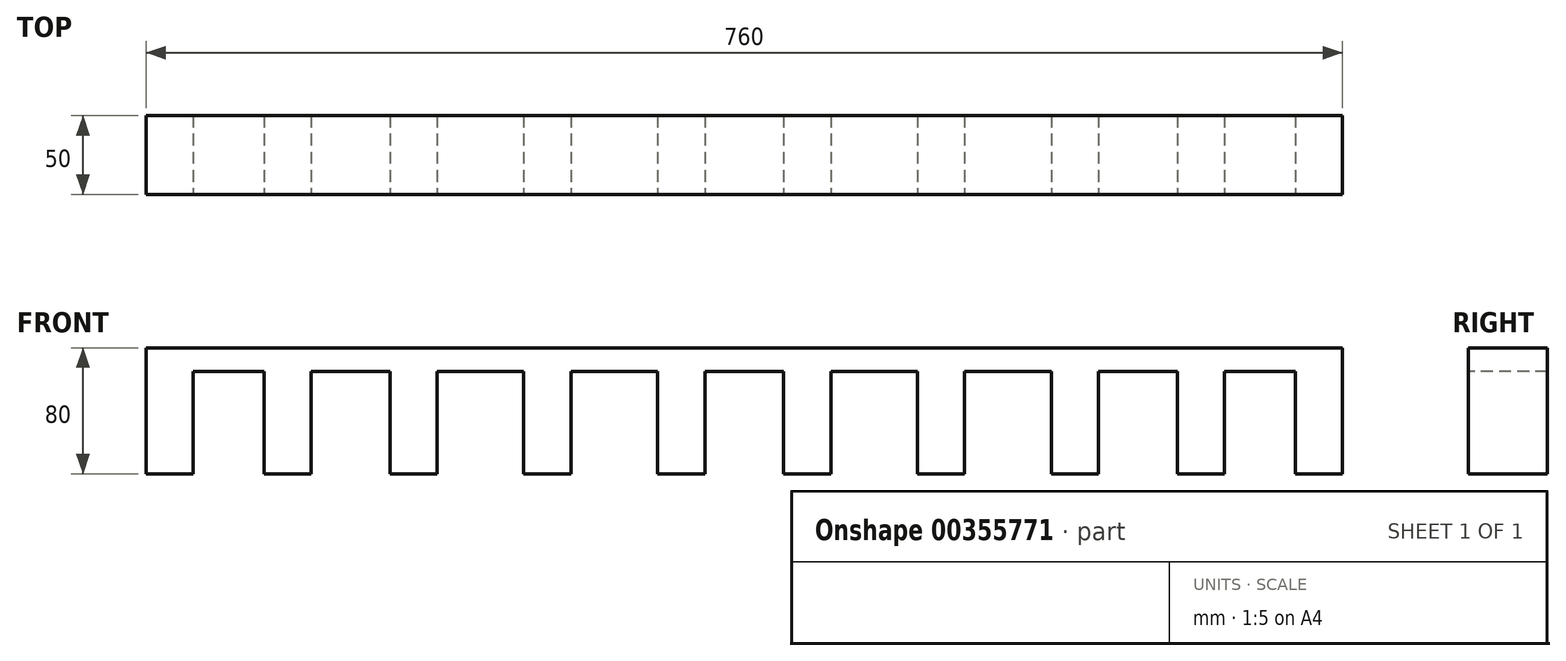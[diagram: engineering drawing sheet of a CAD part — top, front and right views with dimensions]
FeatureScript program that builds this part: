
annotation { "Feature Type Name" : "Feature", "Feature Type Description" : "" }
export const myFeature = defineFeature(function(context is Context, id is Id, definition is map)
    precondition{}
    {
        {
            var Q0;
            Q0=qCreatedBy(makeId("Front.planeOp"),FACE);
            var sketch = newSketch(context, id + "F0", { "sketchPlane" : qUnion([Q0])});
            skLineSegment(sketch, "E0.bottom", {"start": v(-404.78, 0) * mm, "end": v(355.22, 0) * mm});
            skLineSegment(sketch, "E0.top", {"start": v(-404.78, -80) * mm, "end": v(355.22, -80) * mm});
            skLineSegment(sketch, "E0.left", {"start": v(-404.78, 0) * mm, "end": v(-404.78, -80) * mm});
            skLineSegment(sketch, "E0.right", {"start": v(355.22, 0) * mm, "end": v(355.22, -80) * mm});
            skSolve(sketch);
        }
        {
            var Q0;
            Q0=makeQuery(id+"F0.imprint","IMPRINT",FACE,{"disambiguationData":[TD([[makeQuery(id+"F0.imprint","IMPRINT",EDGE,{"derivedFrom":sQuery(id+"F0.wireOp",EDGE,"E0.bottom")}),-1.0]])]});
            extrude(context, id + "F1", {"entities" : qUnion([Q0]), "depth" : 50 * mm});
        }
        {
            var Q0;
            Q0=makeQuery(id+"F1.opExtrude","CAP_FACE",FACE,{"disambiguationData":[OSD([sQuery(id+"F0.wireOp",EDGE,"E0.bottom"),sQuery(id+"F0.wireOp",EDGE,"E0.top"),sQuery(id+"F0.wireOp",EDGE,"E0.left"),sQuery(id+"F0.wireOp",EDGE,"E0.right")])],"isStart":false});
            var sketch = newSketch(context, id + "F2", { "sketchPlane" : qUnion([Q0])});
            skLineSegment(sketch, "E1.bottom", {"start": v(-374.78, -80) * mm, "end": v(-329.78, -80) * mm});
            skLineSegment(sketch, "E1.top", {"start": v(-374.78, -15) * mm, "end": v(-329.78, -15) * mm});
            skLineSegment(sketch, "E1.left", {"start": v(-374.78, -80) * mm, "end": v(-374.78, -15) * mm});
            skLineSegment(sketch, "E1.right", {"start": v(-329.78, -80) * mm, "end": v(-329.78, -15) * mm});
            skLineSegment(sketch, "E2.bottom", {"start": v(-299.78, -80) * mm, "end": v(-249.78, -80) * mm});
            skLineSegment(sketch, "E2.top", {"start": v(-299.78, -15) * mm, "end": v(-249.78, -15) * mm});
            skLineSegment(sketch, "E2.left", {"start": v(-299.78, -80) * mm, "end": v(-299.78, -15) * mm});
            skLineSegment(sketch, "E2.right", {"start": v(-249.78, -80) * mm, "end": v(-249.78, -15) * mm});
            skLineSegment(sketch, "E3.bottom", {"start": v(-219.78, -80) * mm, "end": v(-164.78, -80) * mm});
            skLineSegment(sketch, "E3.top", {"start": v(-219.78, -15) * mm, "end": v(-164.78, -15) * mm});
            skLineSegment(sketch, "E3.left", {"start": v(-219.78, -80) * mm, "end": v(-219.78, -15) * mm});
            skLineSegment(sketch, "E3.right", {"start": v(-164.78, -80) * mm, "end": v(-164.78, -15) * mm});
            skPoint(sketch, "E4.oppositeSnap0", {"position": v(-192.28, -15) * mm});
            skLineSegment(sketch, "E4.bottom", {"start": v(-134.78, -80) * mm, "end": v(-79.78, -80) * mm});
            skLineSegment(sketch, "E4.top", {"start": v(-134.78, -15) * mm, "end": v(-79.78, -15) * mm});
            skLineSegment(sketch, "E4.left", {"start": v(-134.78, -80) * mm, "end": v(-134.78, -15) * mm});
            skLineSegment(sketch, "E4.right", {"start": v(-79.78, -80) * mm, "end": v(-79.78, -15) * mm});
            skLineSegment(sketch, "E5.bottom", {"start": v(-49.78, -80) * mm, "end": v(0.22, -80) * mm});
            skLineSegment(sketch, "E5.top", {"start": v(-49.78, -15) * mm, "end": v(0.22, -15) * mm});
            skLineSegment(sketch, "E5.left", {"start": v(-49.78, -80) * mm, "end": v(-49.78, -15) * mm});
            skLineSegment(sketch, "E5.right", {"start": v(0.22, -80) * mm, "end": v(0.22, -15) * mm});
            skLineSegment(sketch, "E6.bottom", {"start": v(30.22, -80) * mm, "end": v(85.22, -80) * mm});
            skLineSegment(sketch, "E6.top", {"start": v(30.22, -15) * mm, "end": v(85.22, -15) * mm});
            skLineSegment(sketch, "E6.left", {"start": v(30.22, -80) * mm, "end": v(30.22, -15) * mm});
            skLineSegment(sketch, "E6.right", {"start": v(85.22, -80) * mm, "end": v(85.22, -15) * mm});
            skLineSegment(sketch, "E7.bottom", {"start": v(115.22, -80) * mm, "end": v(170.22, -80) * mm});
            skLineSegment(sketch, "E7.top", {"start": v(115.22, -15) * mm, "end": v(170.22, -15) * mm});
            skLineSegment(sketch, "E7.left", {"start": v(115.22, -80) * mm, "end": v(115.22, -15) * mm});
            skLineSegment(sketch, "E7.right", {"start": v(170.22, -80) * mm, "end": v(170.22, -15) * mm});
            skLineSegment(sketch, "E8.bottom", {"start": v(200.22, -80) * mm, "end": v(250.22, -80) * mm});
            skLineSegment(sketch, "E8.top", {"start": v(200.22, -15) * mm, "end": v(250.22, -15) * mm});
            skLineSegment(sketch, "E8.left", {"start": v(200.22, -80) * mm, "end": v(200.22, -15) * mm});
            skLineSegment(sketch, "E8.right", {"start": v(250.22, -80) * mm, "end": v(250.22, -15) * mm});
            skLineSegment(sketch, "E9.bottom", {"start": v(280.22, -80) * mm, "end": v(325.22, -80) * mm});
            skLineSegment(sketch, "E9.top", {"start": v(280.22, -15) * mm, "end": v(325.22, -15) * mm});
            skLineSegment(sketch, "E9.left", {"start": v(280.22, -80) * mm, "end": v(280.22, -15) * mm});
            skLineSegment(sketch, "E9.right", {"start": v(325.22, -80) * mm, "end": v(325.22, -15) * mm});
            skSolve(sketch);
        }
        {
            var Q0;
            Q0=qSketchRegion(id+"F2",true);
            extrude(context, id + "F3", {"entities" : qUnion([Q0]), "operationType" : NewBodyOperationType.REMOVE, "oppositeDirection" : true, "depth" : 50 * mm});
        }
    });
